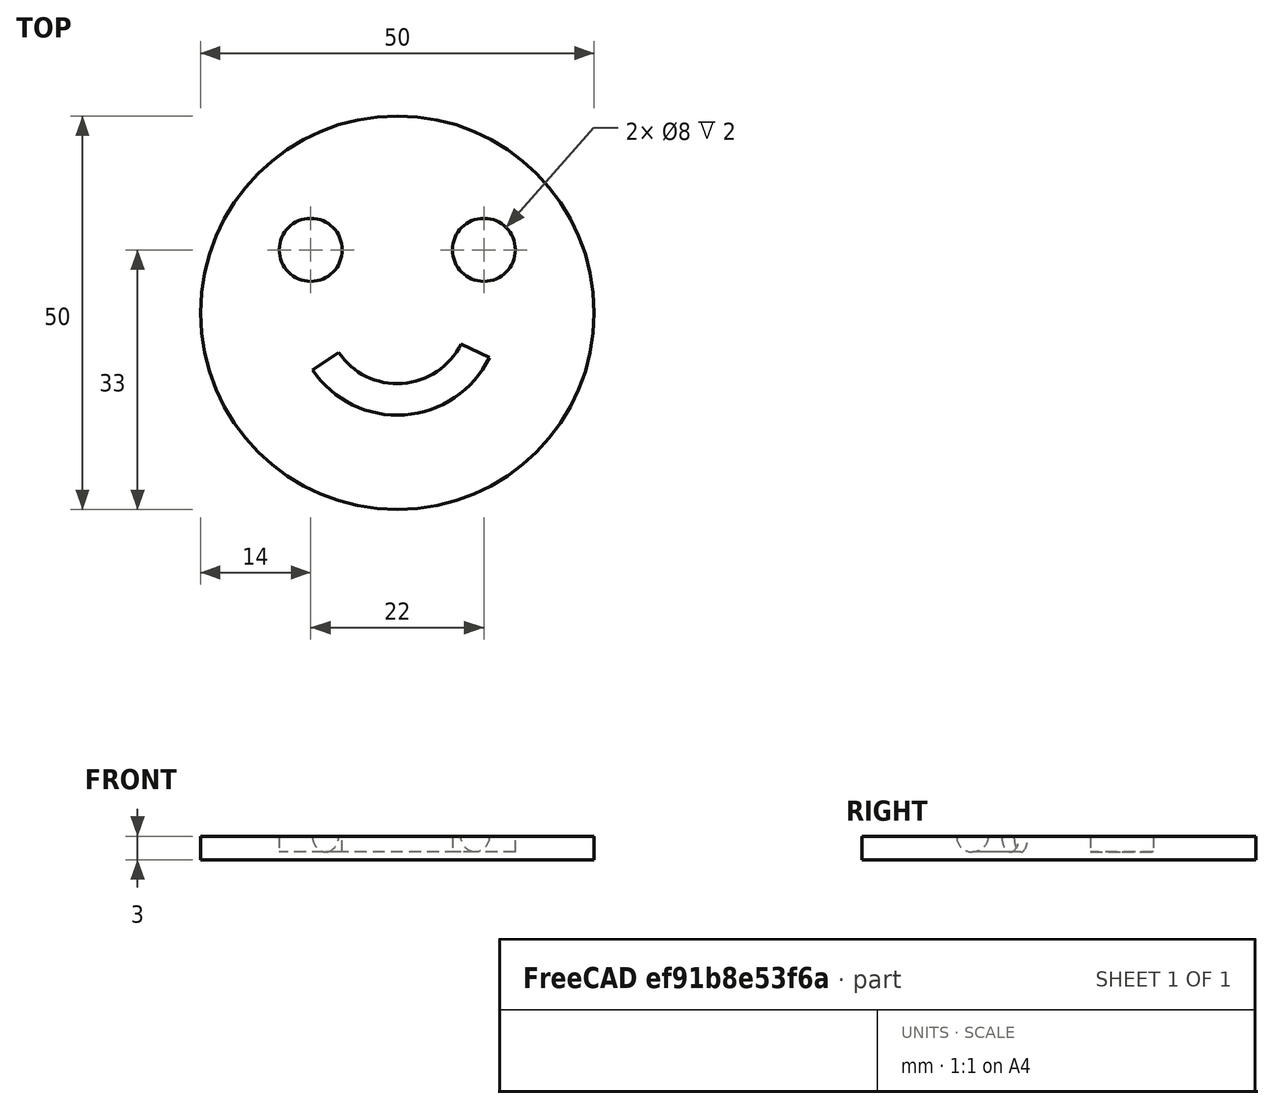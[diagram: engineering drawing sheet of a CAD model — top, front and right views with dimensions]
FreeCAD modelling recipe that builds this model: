
FCSTD DOCUMENT  (FreeCAD 0.21R33694 (Git))
Label: OJT1_T15R01_cara
License: All rights reserved
LicenseURL: http://en.wikipedia.org/wiki/All_rights_reserved
objects: Part::Cylinder×3, Part::Cut×3, Part::Torus×1
note: 7 computed .brp shape members not serialized (recipe doc carries the construction recipe); baked Part::Feature solids carry a one-line shape summary decoded from their .brp

FEATURE [Part::Cylinder] Cylinder  label="base"
  Angle = 360
  AttacherType = Attacher::AttachEngine3D
  FirstAngle = 0
  Height = 3
  Radius = 25
  SecondAngle = 0
FEATURE [Part::Torus] Torus  label="boca"
  Angle1 = -180
  Angle2 = 180
  Angle3 = 120
  AttacherType = Attacher::AttachEngine3D
  Placement = pos=(0,0,3) rot=(0,0,-1;2.54818rad)
  Radius1 = 11
  Radius2 = 2
FEATURE [Part::Cylinder] Cylinder001  label="ull1"
  Angle = 360
  AttacherType = Attacher::AttachEngine3D
  FirstAngle = 0
  Height = 2
  Placement = pos=(11,8,1) rot=(0,0,1;0rad)
  Radius = 4
  SecondAngle = 0
FEATURE [Part::Cylinder] Cylinder002  label="ull2"
  Angle = 360
  AttacherType = Attacher::AttachEngine3D
  FirstAngle = 0
  Height = 2
  Placement = pos=(-11,8,1) rot=(0,0,1;0rad)
  Radius = 4
  SecondAngle = 0
FEATURE [Part::Cut] Cut
  Base = -> Cylinder
  Refine = true
  Tool = -> Torus
FEATURE [Part::Cut] Cut001
  Base = -> Cut
  Refine = true
  Tool = -> Cylinder002
FEATURE [Part::Cut] Cut002
  Base = -> Cut001
  Refine = true
  Tool = -> Cylinder001
